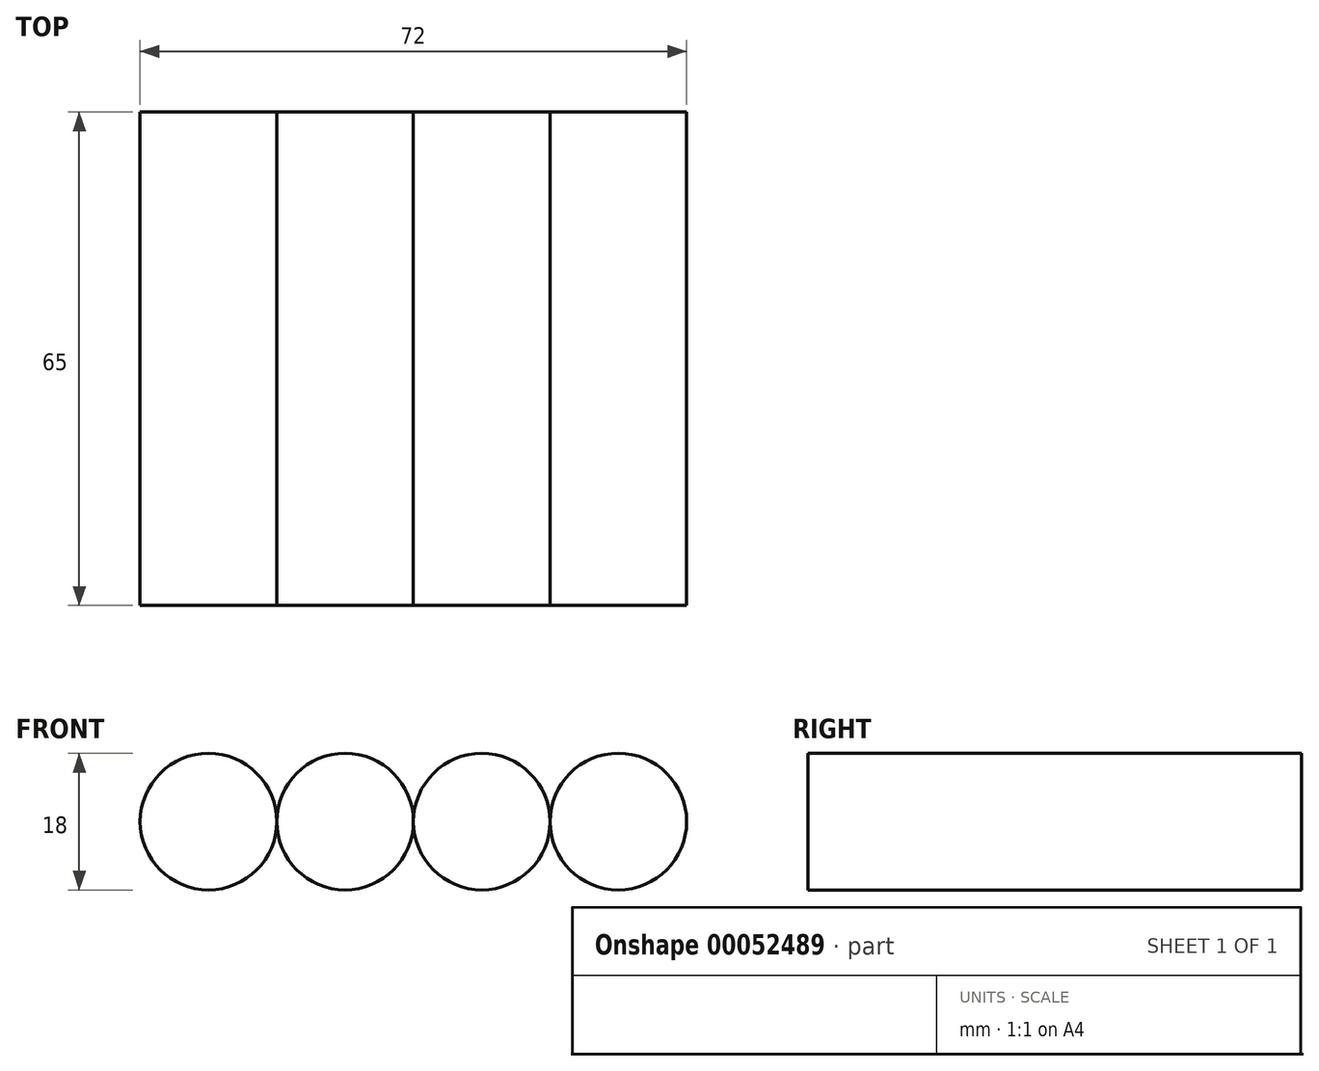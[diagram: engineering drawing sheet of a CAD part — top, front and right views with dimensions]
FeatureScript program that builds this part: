
annotation { "Feature Type Name" : "Feature", "Feature Type Description" : "" }
export const myFeature = defineFeature(function(context is Context, id is Id, definition is map)
    precondition{}
    {
        {
            var Q0;
            Q0=qCreatedBy(makeId("Front.planeOp"),FACE);
            var sketch = newSketch(context, id + "F0", { "sketchPlane" : qUnion([Q0])});
            skCircle(sketch, "E0", {"center": v(-42.16, 0) * mm, "radius": 9 * mm});
            skCircle(sketch, "E1", {"center": v(-24.16, 0) * mm, "radius": 9 * mm});
            skCircle(sketch, "E2", {"center": v(-6.16, 0) * mm, "radius": 9 * mm});
            skCircle(sketch, "E3", {"center": v(11.84, 0) * mm, "radius": 9 * mm});
            skSolve(sketch);
        }
        {
            var Q0;
            Q0=makeQuery(id+"F0.imprint","IMPRINT",FACE,{"disambiguationData":[TD([[makeQuery(id+"F0.imprint","IMPRINT",EDGE,{"derivedFrom":sQuery(id+"F0.wireOp",EDGE,"E0")}),1.0]])]});
            var Q1;
            {var subQ0=sQuery(id+"F0.wireOp",EDGE,"E1");var subQ1=makeQuery(id+"F0.imprint","INTERSECT",VERTEX,{"derivedFrom":[sQuery(id+"F0.wireOp",EDGE,"E0"),subQ0]});Q1=makeQuery(id+"F0.imprint","IMPRINT",FACE,{"disambiguationData":[TD([[makeQuery(id+"F0.imprint","IMPRINT",EDGE,{"disambiguationData":[TD([[subQ1,1.0]])],"derivedFrom":subQ0}),1.0]])]});}
            var Q2;
            {var subQ0=sQuery(id+"F0.wireOp",EDGE,"E2");var subQ1=makeQuery(id+"F0.imprint","INTERSECT",VERTEX,{"derivedFrom":[sQuery(id+"F0.wireOp",EDGE,"E1"),subQ0]});Q2=makeQuery(id+"F0.imprint","IMPRINT",FACE,{"disambiguationData":[TD([[makeQuery(id+"F0.imprint","IMPRINT",EDGE,{"disambiguationData":[TD([[subQ1,1.0]])],"derivedFrom":subQ0}),1.0]])]});}
            var Q3;
            Q3=makeQuery(id+"F0.imprint","IMPRINT",FACE,{"disambiguationData":[TD([[makeQuery(id+"F0.imprint","IMPRINT",EDGE,{"derivedFrom":sQuery(id+"F0.wireOp",EDGE,"E3")}),1.0]])]});
            extrude(context, id + "F1", {"entities" : qUnion([Q0, Q1, Q2, Q3]), "depth" : 65 * mm});
        }
    });
